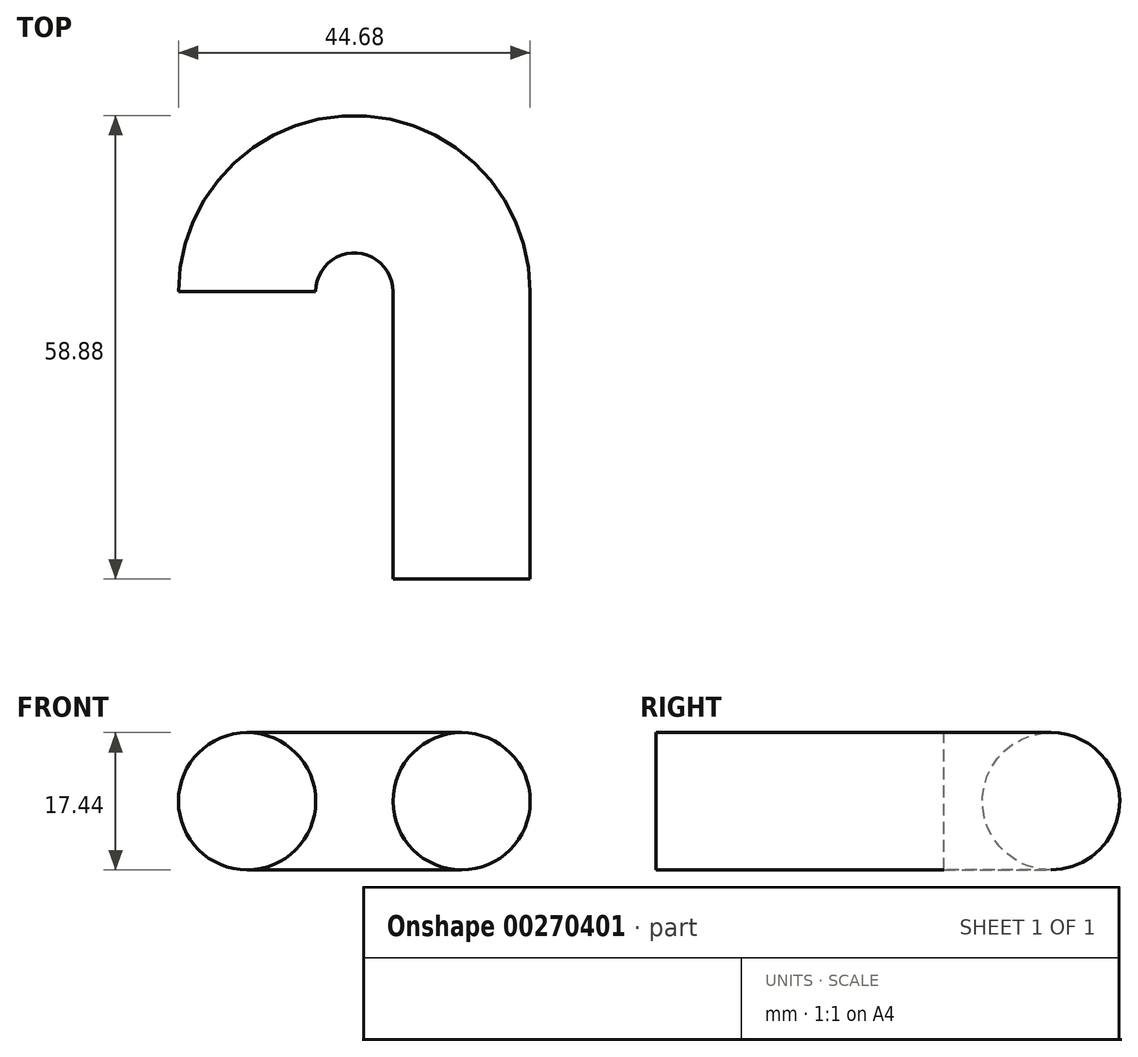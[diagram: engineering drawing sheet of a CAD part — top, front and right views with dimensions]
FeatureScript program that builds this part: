
annotation { "Feature Type Name" : "Feature", "Feature Type Description" : "" }
export const myFeature = defineFeature(function(context is Context, id is Id, definition is map)
    precondition{}
    {
        {
            var Q0;
            Q0=qCreatedBy(makeId("Top.planeOp"),FACE);
            var sketch = newSketch(context, id + "F0", { "sketchPlane" : qUnion([Q0])});
            skLineSegment(sketch, "E0", {"start": v(0, 0) * mm, "end": v(0, 36.54) * mm});
            skArc(sketch, "E1", {"start": v(0, 36.54) * mm, "mid": v(-13.62, 50.16) * mm, "end": v(-27.24, 36.54) * mm});
            skSolve(sketch);
        }
        {
            var Q0;
            Q0=qCreatedBy(makeId("Front.planeOp"),FACE);
            var sketch = newSketch(context, id + "F1", { "sketchPlane" : qUnion([Q0])});
            skPoint(sketch, "E2.0.midPoint", {"position": v(6.76, 0) * mm});
            skCircle(sketch, "E3", {"center": v(0, 0) * mm, "radius": 8.72 * mm});
            skSolve(sketch);
        }
        {
            var Q0;
            Q0=makeQuery(id+"F1.imprint","IMPRINT",FACE,{"disambiguationData":[TD([[makeQuery(id+"F1.imprint","IMPRINT",EDGE,{"derivedFrom":sQuery(id+"F1.wireOp",EDGE,"E3")}),1.0]])]});
            var Q1;
            Q1=sQuery(id+"F0.wireOp",EDGE,"E0");
            var Q2;
            Q2=sQuery(id+"F0.wireOp",EDGE,"E1");
            sweep(context, id + "F2", {"profiles" : qUnion([Q0]), "path" : qUnion([Q1, Q2])});
        }
    });
